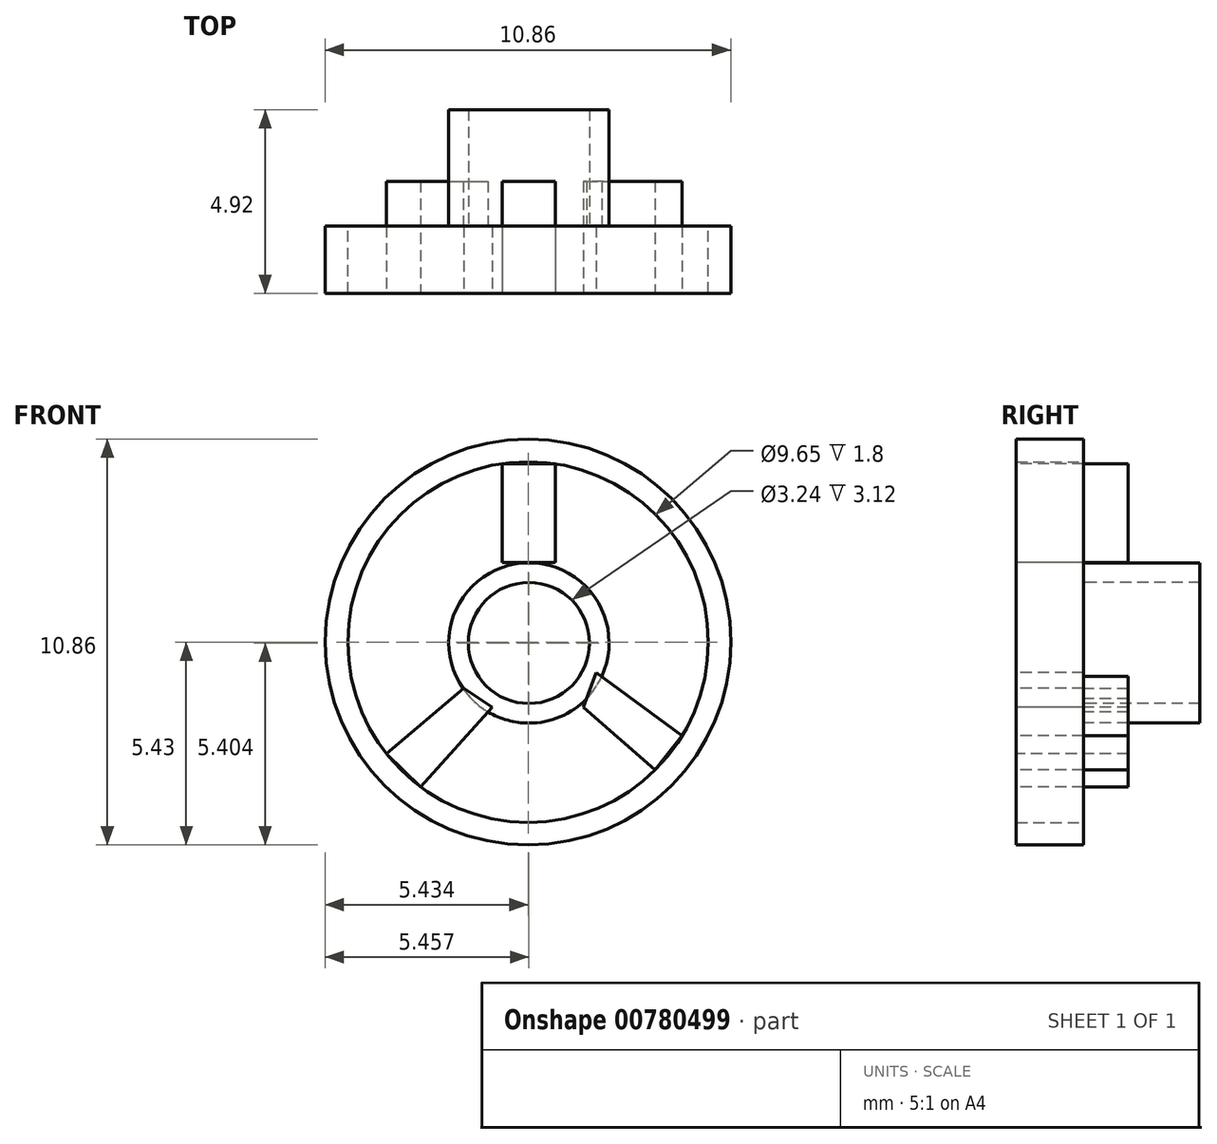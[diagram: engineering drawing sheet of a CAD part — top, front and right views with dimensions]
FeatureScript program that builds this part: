
annotation { "Feature Type Name" : "Feature", "Feature Type Description" : "" }
export const myFeature = defineFeature(function(context is Context, id is Id, definition is map)
    precondition{}
    {
        {
            var Q0;
            Q0=qCreatedBy(makeId("Front.planeOp"),FACE);
            var sketch = newSketch(context, id + "F0", { "sketchPlane" : qUnion([Q0])});
            skCircle(sketch, "E0", {"center": v(-36.45, 10.03) * mm, "radius": 2.15 * mm});
            skCircle(sketch, "E1", {"center": v(-36.45, 10.03) * mm, "radius": 1.62 * mm});
            skPoint(sketch, "E2.start.orphan", {"position": v(-37.73, 8.31) * mm});
            skPoint(sketch, "E3.trimOffspring.end.orphan", {"position": v(-37.73, 5.57) * mm});
            skSolve(sketch);
        }
        {
            var Q0;
            Q0 = qSketchRegion(id + "F0", true);
            extrude(context, id + "F1", {"entities" : qUnion([Q0]), "oppositeDirection" : true, "depth" : 3.12 * mm, "offsetDistance" : 25 * mm});
        }
        {
            var Q0;
            Q0=qCreatedBy(makeId("Front.planeOp"),FACE);
            var sketch = newSketch(context, id + "F2", { "sketchPlane" : qUnion([Q0])});
            skCircle(sketch, "E4", {"center": v(-36.48, 10.06) * mm, "radius": 5.43 * mm});
            skCircle(sketch, "E5", {"center": v(-36.48, 10.06) * mm, "radius": 4.83 * mm});
            skSolve(sketch);
        }
        {
            var Q0;
            Q0 = qSketchRegion(id + "F2", true);
            extrude(context, id + "F3", {"entities" : qUnion([Q0]), "depth" : 1.8 * mm, "offsetDistance" : 25 * mm});
        }
        {
            var Q0;
            Q0=makeQuery(id+"F3.opExtrude","CAP_FACE",FACE,{"disambiguationData":[OSD([sQuery(id+"F2.wireOp",EDGE,"E4"),sQuery(id+"F2.wireOp",EDGE,"E5")])],"isStart":false});
            var sketch = newSketch(context, id + "F4", { "sketchPlane" : qUnion([Q0])});
            skLineSegment(sketch, "E6", {"start": v(-37.16, 14.84) * mm, "end": v(-37.16, 12.2) * mm});
            skLineSegment(sketch, "E7", {"start": v(-37.16, 12.2) * mm, "end": v(-35.75, 12.2) * mm});
            skLineSegment(sketch, "E8", {"start": v(-35.75, 12.2) * mm, "end": v(-35.75, 14.83) * mm});
            skLineSegment(sketch, "E9", {"start": v(-35.75, 14.83) * mm, "end": v(-37.16, 14.84) * mm});
            skLineSegment(sketch, "E10", {"start": v(-40.27, 7.07) * mm, "end": v(-38.2, 8.82) * mm});
            skLineSegment(sketch, "E11", {"start": v(-34.66, 9.25) * mm, "end": v(-32.35, 7.55) * mm});
            skLineSegment(sketch, "E12", {"start": v(-32.35, 7.55) * mm, "end": v(-33.07, 6.64) * mm});
            skLineSegment(sketch, "E13", {"start": v(-33.07, 6.64) * mm, "end": v(-35, 8.32) * mm});
            skLineSegment(sketch, "E14", {"start": v(-35, 8.32) * mm, "end": v(-34.66, 9.25) * mm});
            skLineSegment(sketch, "E15", {"start": v(-40.27, 7.07) * mm, "end": v(-39.35, 6.19) * mm});
            skLineSegment(sketch, "E16", {"start": v(-39.35, 6.19) * mm, "end": v(-37.43, 8.32) * mm});
            skLineSegment(sketch, "E17", {"start": v(-37.43, 8.32) * mm, "end": v(-38.2, 8.82) * mm});
            skSolve(sketch);
        }
        {
            var Q0;
            Q0 = qSketchRegion(id + "F4", true);
            extrude(context, id + "F5", {"entities" : qUnion([Q0]), "operationType" : NewBodyOperationType.ADD, "oppositeDirection" : true, "depth" : 3 * mm, "offsetDistance" : 25 * mm});
        }
    });
